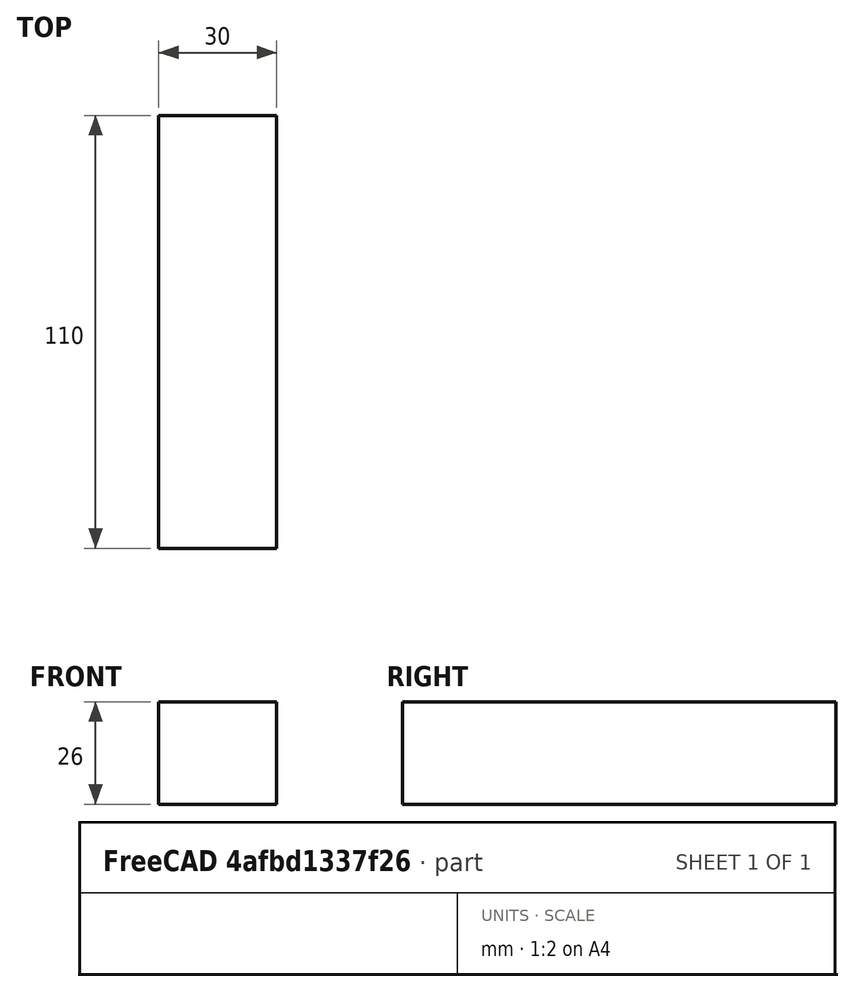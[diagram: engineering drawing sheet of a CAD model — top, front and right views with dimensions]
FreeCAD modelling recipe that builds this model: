
FCSTD DOCUMENT  (FreeCAD 0.18.3R)
Label: CalePanneauCommande
License: All rights reserved
LicenseURL: http://en.wikipedia.org/wiki/All_rights_reserved
objects: Drawing::FeatureViewPython×3, Drawing::FeatureViewPart×2, Part::Box×1, Drawing::FeaturePage×1
note: 1 computed .brp shape members not serialized (recipe doc carries the construction recipe); baked Part::Feature solids carry a one-line shape summary decoded from their .brp

FEATURE [Part::Box] Box  label="Cube"
  AttacherType = Attacher::AttachEngine3D
  Height = 26
  Length = 30
  Width = 110
FEATURE [Drawing::FeatureViewPart] Ortho  label="Ortho_0_0"
  Direction = (1,0,0)
  HiddenWidth = 0.15
  LineWidth = 0.35
  Rotation = -90
  Scale = 1.5
  ShowHiddenLines = false
  ShowSmoothLines = false
  Source = -> Box
  Tolerance = 0.05
  ViewResult = <g id="Ortho_0_0"\n   transform="rotate(-90,42.3333,108.5) translate(42.3333,108.5) scale(1.5,1.5)"\n  >\n<g   fill="none"\n   stroke="rgb(0, 0, 0)"\n   stroke-linecap="butt"\n   stroke-linejoin="miter"\n   stroke-width="0.233333"\n   transform="scale(1,-1)"\n  >\n<path id= "1" d=" M 0 0 L 26 0 " />\n<path id= "2" d=" M 26 0 L 26 -125 " />\n<path id= "3" d=" M 0 -125 L 26 -125 " />\n<path id= "4" d=" M 0 0 L 0 -125 " />\n</g>\n</g>
  Visible = false
  X = 42.3333
  Y = 108.5
FEATURE [Drawing::FeatureViewPart] Ortho001  label="Ortho_1_0"
  Direction = (0,-1,0)
  HiddenWidth = 0.15
  LineWidth = 0.35
  Rotation = 90
  Scale = 1.5
  ShowHiddenLines = false
  ShowSmoothLines = false
  Source = -> Box
  Tolerance = 0.05
  ViewResult = <g id="Ortho_1_0"\n   transform="rotate(90,209.667,108.5) translate(209.667,108.5) scale(1.5,1.5)"\n  >\n<g   fill="none"\n   stroke="rgb(0, 0, 0)"\n   stroke-linecap="butt"\n   stroke-linejoin="miter"\n   stroke-width="0.233333"\n   transform="scale(1,-1)"\n  >\n<path id= "1" d=" M 0 0 L -26 0 " />\n<path id= "2" d=" M 0 30 L -26 30 " />\n<path id= "3" d=" M 0 0 L 0 30 " />\n<path id= "4" d=" M -26 0 L -26 30 " />\n</g>\n</g>
  Visible = false
  X = 209.667
  Y = 108.5
FEATURE [Drawing::FeatureViewPython] dim001  # drawing view (typed FeaturePython)
  Rotation = 0
  ViewResult = <g> \n  <line x1="42.333300" y1="67.500000" x2="42.333300" y2="48.133333" style="stroke:rgb(0,0,255);stroke-width:0.30" />\n<line x1="177.333300" y1="67.500000" x2="177.333300" y2="48.133333" style="stroke:rgb(0,0,255);stroke-width:0.30" />\n<line x1="42.333300" y1="49.133333" x2="177.333300" y2="49.133333" style="stroke:rgb(0,0,255);stroke-width:0.30" /> \n  <polygon points="177.333300,49.133333 174.333300,48.133333 173.333300,49.133333 174.333300,50.133333" style="fill:rgb(0,0,255);stroke:rgb(0,0,255);stroke-width:0" /><polygon points="42.333300,49.133333 45.333300,50.133333 46.333300,49.133333 45.333300,48.133333" style="fill:rgb(0,0,255);stroke:rgb(0,0,255);stroke-width:0" /> \n  <text x="109.833300" y="47.133333" font-family="Verdana" font-size="3.6" fill="rgb(0,0,255)" text-anchor="middle" transform="rotate(0.000000 109.833300,47.133333)" > 90</text> </g>
  Visible = true
  X = 0
  Y = 0
  arrowL1 = 3
  arrowL2 = 1
  arrowW = 2
  arrow_scheme = 0
  autoPlaceOffset = 2
  autoPlaceText = true
  click1_x = 125
  click1_y = 49.1333
  click2_x = 125
  click2_y = 49.1333
  comma_decimal_place = false
  dimension_line_overshoot = 1
  gap_datum_points = 2
  halfDimension_linear = false
  lineColor = rgb(0,0,255)
  strokeWidth = 0.3
  textFormat_linear = %(value)3.0f
  textRenderer_color = rgb(0,0,255)
  textRenderer_family = Verdana
  textRenderer_size = 3.6
  unit_custom_scale = 1
  unit_scheme = 0
FEATURE [Drawing::FeatureViewPython] dim002  # drawing view (typed FeaturePython)
  Rotation = 0
  ViewResult = <g> \n  <line x1="256.667000" y1="108.500000" x2="281.000000" y2="108.500000" style="stroke:rgb(0,0,255);stroke-width:0.30" />\n<line x1="256.667000" y1="69.500000" x2="281.000000" y2="69.500000" style="stroke:rgb(0,0,255);stroke-width:0.30" />\n<line x1="280.000000" y1="108.500000" x2="280.000000" y2="69.500000" style="stroke:rgb(0,0,255);stroke-width:0.30" /> \n  <polygon points="280.000000,69.500000 279.000000,72.500000 280.000000,73.500000 281.000000,72.500000" style="fill:rgb(0,0,255);stroke:rgb(0,0,255);stroke-width:0" /><polygon points="280.000000,108.500000 281.000000,105.500000 280.000000,104.500000 279.000000,105.500000" style="fill:rgb(0,0,255);stroke:rgb(0,0,255);stroke-width:0" /> \n  <text x="278.000000" y="89.000000" font-family="Verdana" font-size="3.6" fill="rgb(0,0,255)" text-anchor="middle" transform="rotate(-90.000000 278.000000,89.000000)" > 26</text> </g>
  Visible = true
  X = 0
  Y = 0
  arrowL1 = 3
  arrowL2 = 1
  arrowW = 2
  arrow_scheme = 0
  autoPlaceOffset = 2
  autoPlaceText = true
  click1_x = 280
  click1_y = 88.1333
  click2_x = 280
  click2_y = 88.1333
  comma_decimal_place = false
  dimension_line_overshoot = 1
  gap_datum_points = 2
  halfDimension_linear = false
  lineColor = rgb(0,0,255)
  strokeWidth = 0.3
  textFormat_linear = %(value)3.0f
  textRenderer_color = rgb(0,0,255)
  textRenderer_family = Verdana
  textRenderer_size = 3.6
  unit_custom_scale = 1
  unit_scheme = 0
FEATURE [Drawing::FeatureViewPython] dim003  # drawing view (typed FeaturePython)
  Rotation = 0
  ViewResult = <g> \n  <line x1="209.667000" y1="67.500000" x2="209.667000" y2="48.133333" style="stroke:rgb(0,0,255);stroke-width:0.30" />\n<line x1="254.667000" y1="67.500000" x2="254.667000" y2="48.133333" style="stroke:rgb(0,0,255);stroke-width:0.30" />\n<line x1="209.667000" y1="49.133333" x2="254.667000" y2="49.133333" style="stroke:rgb(0,0,255);stroke-width:0.30" /> \n  <polygon points="254.667000,49.133333 251.667000,48.133333 250.667000,49.133333 251.667000,50.133333" style="fill:rgb(0,0,255);stroke:rgb(0,0,255);stroke-width:0" /><polygon points="209.667000,49.133333 212.667000,50.133333 213.667000,49.133333 212.667000,48.133333" style="fill:rgb(0,0,255);stroke:rgb(0,0,255);stroke-width:0" /> \n  <text x="232.167000" y="47.133333" font-family="Verdana" font-size="3.6" fill="rgb(0,0,255)" text-anchor="middle" transform="rotate(0.000000 232.167000,47.133333)" > 30</text> </g>
  Visible = true
  X = 0
  Y = 0
  arrowL1 = 3
  arrowL2 = 1
  arrowW = 2
  arrow_scheme = 0
  autoPlaceOffset = 2
  autoPlaceText = true
  click1_x = 230
  click1_y = 49.1333
  click2_x = 230
  click2_y = 49.1333
  comma_decimal_place = false
  dimension_line_overshoot = 1
  gap_datum_points = 2
  halfDimension_linear = false
  lineColor = rgb(0,0,255)
  strokeWidth = 0.3
  textFormat_linear = %(value)3.0f
  textRenderer_color = rgb(0,0,255)
  textRenderer_family = Verdana
  textRenderer_size = 3.6
  unit_custom_scale = 1
  unit_scheme = 0
FEATURE [Drawing::FeaturePage] Page
  EditableTexts = GB | Cale panneau cmde | 6 exemplaires | A4 | X / Y | 15/10 | PN | DN | DD/MM/YYYY | REV A
  Group = -> [Ortho,Ortho001,dim001,dim002,dim003]
  Template = <path>
note: 1 file-system path scrubbed to <path> (originals preserved in the JSON sidecar)
